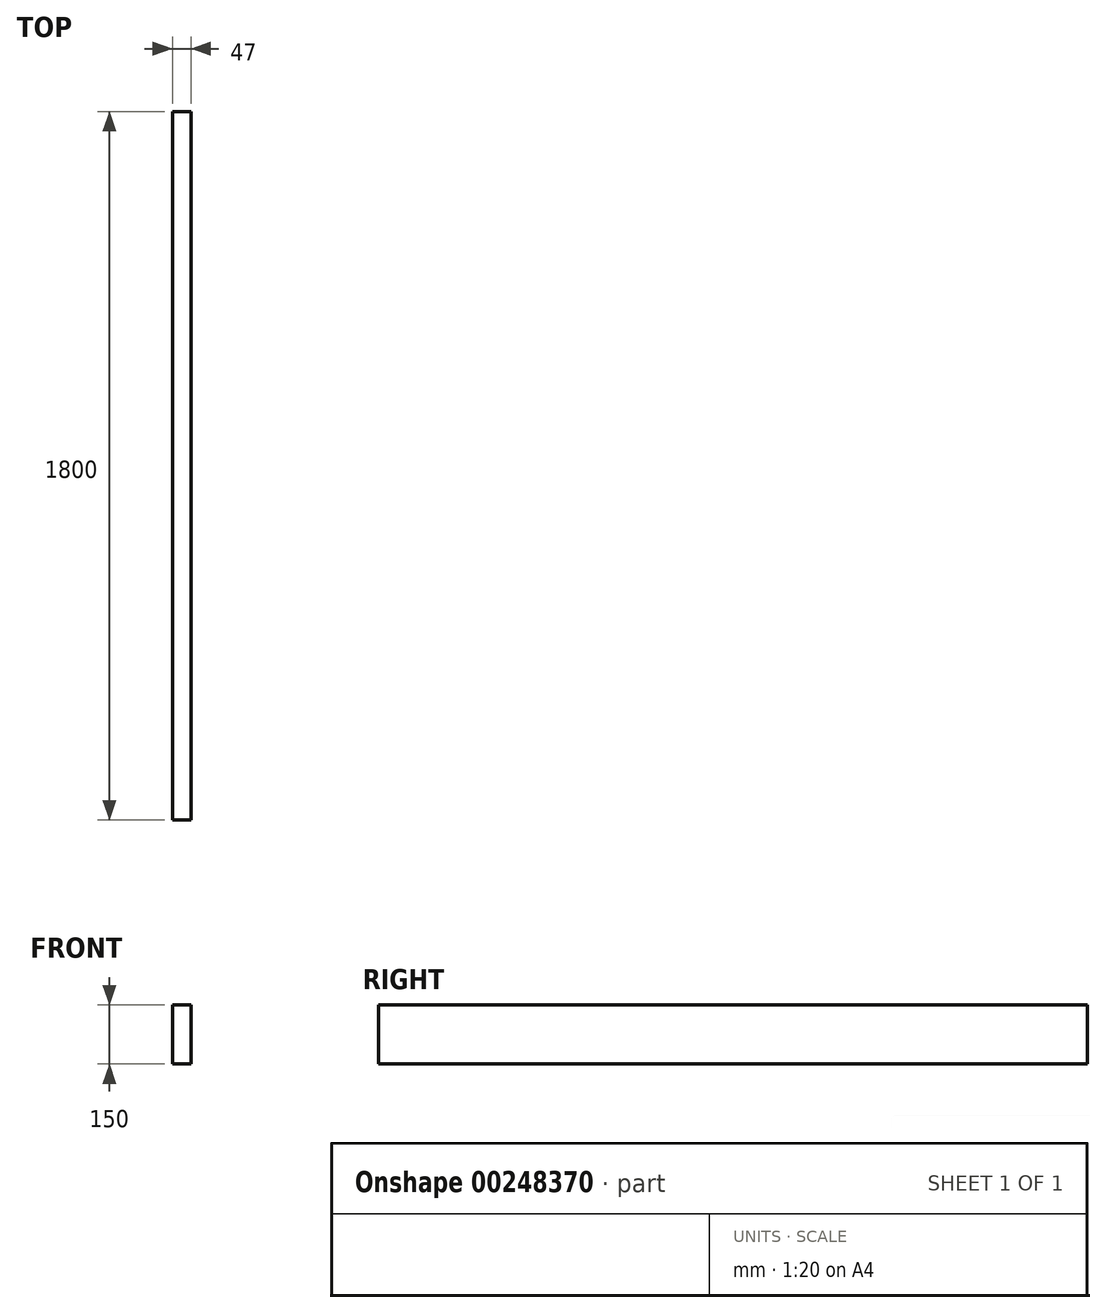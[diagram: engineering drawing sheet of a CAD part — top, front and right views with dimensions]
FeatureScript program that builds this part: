
annotation { "Feature Type Name" : "Feature", "Feature Type Description" : "" }
export const myFeature = defineFeature(function(context is Context, id is Id, definition is map)
    precondition{}
    {
        {
            var Q0;
            Q0=qCreatedBy(makeId("Front.planeOp"),FACE);
            var sketch = newSketch(context, id + "F0", { "sketchPlane" : qUnion([Q0])});
            skLineSegment(sketch, "E0.bottom", {"start": v(0, 0) * mm, "end": v(47, 0) * mm});
            skLineSegment(sketch, "E0.top", {"start": v(0, 150) * mm, "end": v(47, 150) * mm});
            skLineSegment(sketch, "E0.left", {"start": v(0, 0) * mm, "end": v(0, 150) * mm});
            skLineSegment(sketch, "E0.right", {"start": v(47, 0) * mm, "end": v(47, 150) * mm});
            skSolve(sketch);
        }
        {
            var Q0;
            Q0 = qSketchRegion(id + "F0", true);
            extrude(context, id + "F1", {"entities" : qUnion([Q0]), "oppositeDirection" : true, "depth" : 1800 * mm});
        }
    });
